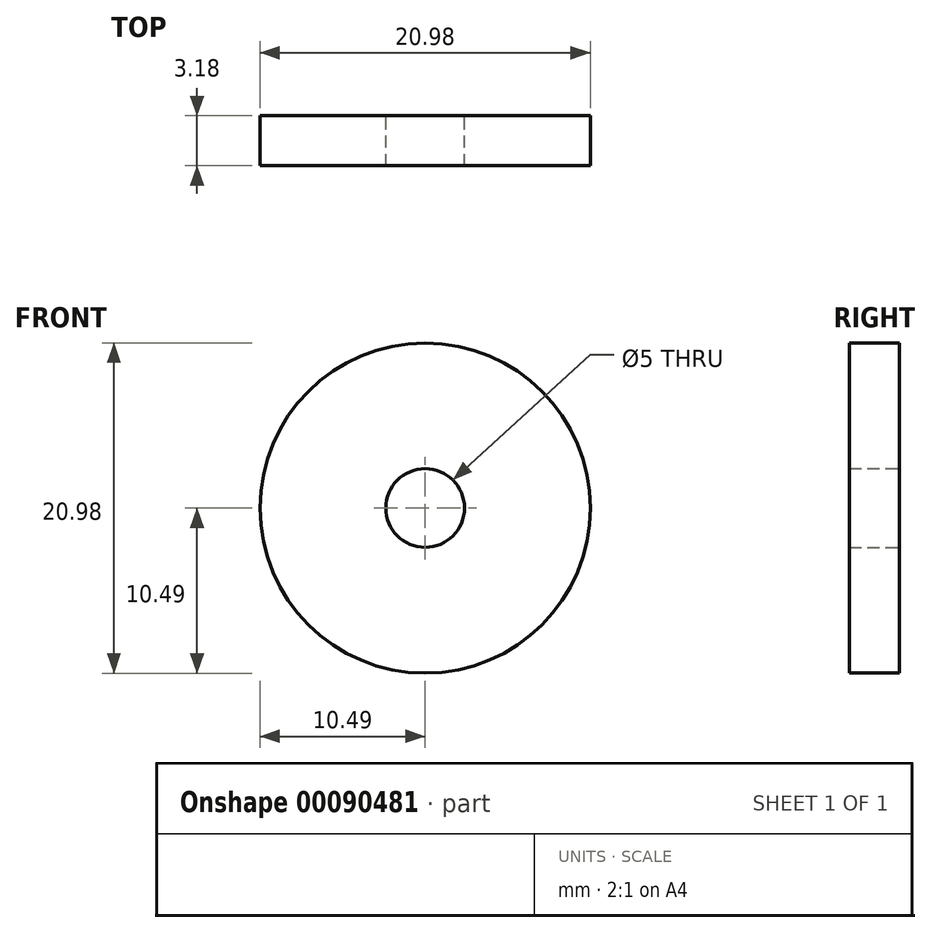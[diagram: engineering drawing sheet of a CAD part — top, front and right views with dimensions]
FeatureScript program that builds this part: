
annotation { "Feature Type Name" : "Feature", "Feature Type Description" : "" }
export const myFeature = defineFeature(function(context is Context, id is Id, definition is map)
    precondition{}
    {
        {
            var Q0;
            Q0=qCreatedBy(makeId("Front.planeOp"),FACE);
            var sketch = newSketch(context, id + "F0", { "sketchPlane" : qUnion([Q0])});
            skCircle(sketch, "E0", {"center": v(0, 0) * mm, "radius": 10.49 * mm});
            skSolve(sketch);
        }
        {
            var Q0;
            Q0 = qSketchRegion(id + "F0", true);
            extrude(context, id + "F1", {"entities" : qUnion([Q0]), "depth" : 3.17 * mm});
        }
        {
            var Q0;
            Q0=makeQuery(id+"F1.opExtrude","CAP_FACE",FACE,{"disambiguationData":[OSD([sQuery(id+"F0.wireOp",EDGE,"E0")])],"isStart":true});
            var sketch = newSketch(context, id + "F2", { "sketchPlane" : qUnion([Q0])});
            skCircle(sketch, "E1", {"center": v(0, 0) * mm, "radius": 3.16 * mm});
            skSolve(sketch);
        }
        {
            var Q0;
            Q0=sQuery(id+"F2.wireOp",VERTEX,"E1.center");
            var Q1;
            Q1=makeQuery(id+"F1.opExtrude","SWEPT_BODY",BODY,{"disambiguationData":[OSD([sQuery(id+"F0.wireOp",EDGE,"E0")])]});
            hole(context, id + "F3", {"style" : HoleStyle.SIMPLE, "endStyle" : HoleEndStyle.THROUGH, "holeDiameter" : 5 * mm, "locations" : qUnion([Q0]), "scope" : qUnion([Q1]), "isTappedThrough" : true});
        }
    });
